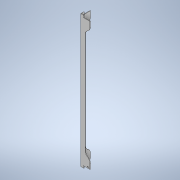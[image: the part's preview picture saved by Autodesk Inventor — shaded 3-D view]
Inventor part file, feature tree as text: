
AUTODESK INVENTOR PART (.ipt)
format: ipt  version: 2022 (Build 260153000, 153)  size: 238,592 bytes
history: native  units: mm
features: extrude x7, sketch x7, chamfer x2, projected_geometry x2, other x1
ambient origin geometry x8: Origin, YZ Plane, XZ Plane, XY Plane, X Axis, Y Axis, Z Axis, Center Point
bodies: Solid1 (feature_tree)
feature tree (19):
  extrude  "Extrusion1"  Depth=1.0mm TaperAngle=45.0deg
  chamfer  "Chamfer1"  Distance=1.2mm
  extrude  "Extrusion2"  Depth=1.2mm TaperAngle=0.0deg
  extrude  "Extrusion3"  Depth=6.5mm TaperAngle=0.0deg
  extrude  "Extrusion4"  Depth=1.0mm
  extrude  "Extrusion5"  Depth=3.2mm
  extrude  "Extrusion6"  [1 undecoded]
  chamfer  "Chamfer2"  [1 undecoded]
  extrude  "Extrusion7"  [1 undecoded]
  sketch  "Sketch1"  dims[d0=12.5mm d1=0.0mm d2=1.0mm d3=2.0mm d4=45.0deg d5=1.2mm d6=0.0mm]
  projected_geometry  "Projected Loop1"
  sketch  "Sketch2"  dims[d7=1.2mm d8=0.0mm d9=1.2mm d10=0.0mm]
  sketch  "Sketch3"  dims[d11=1.2mm d12=0.0mm d13=6.5mm d14=7.0mm d15=0.0mm d16=0.0mm]
  sketch  "Sketch4"  dims[d17=1.0mm d18=2.0mm d19=45.0deg d20=3.0mm]
  sketch  "Sketch5"  dims[d21=19.5mm d22=3.2mm]
  sketch  "Sketch6"  dims[d23=6.5mm d24=0.0mm]
  projected_geometry  "Projected Loop2"
  sketch  "Sketch7"
  other  "Ñêðóãëåíèå2"
note: 3 required parameter values undecoded (feature->parameter linkage not recoverable at this tier; creation-order binding heuristic only, values carry confidence <= 0.55)
